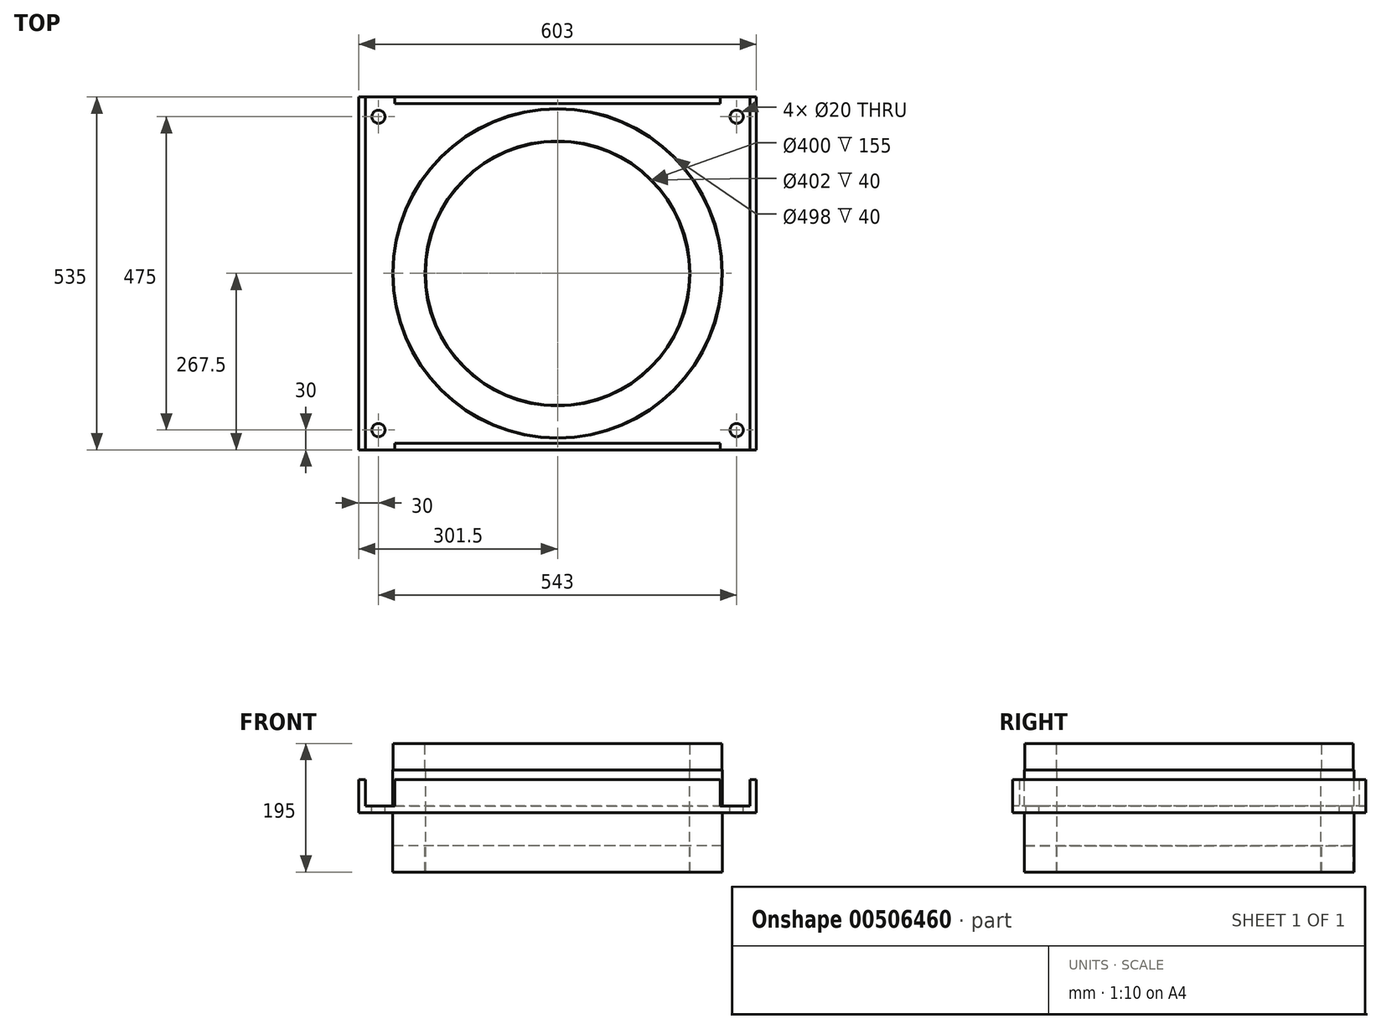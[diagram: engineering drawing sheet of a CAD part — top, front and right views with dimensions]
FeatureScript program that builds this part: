
annotation { "Feature Type Name" : "Feature", "Feature Type Description" : "" }
export const myFeature = defineFeature(function(context is Context, id is Id, definition is map)
    precondition{}
    {
        {
            var Q0;
            Q0=qCreatedBy(makeId("Front.planeOp"),FACE);
            var sketch = newSketch(context, id + "F0", { "sketchPlane" : qUnion([Q0])});
            skLineSegment(sketch, "E0", {"start": v(0, 74.87) * mm, "end": v(0, -73.71) * mm, "construction": true});
            skLineSegment(sketch, "E1", {"start": v(0, 374.84) * mm, "end": v(0, -528.94) * mm, "construction": true});
            skLineSegment(sketch, "E2", {"start": v(-200, -100) * mm, "end": v(-200, 55) * mm});
            skLineSegment(sketch, "E3", {"start": v(-200, 55) * mm, "end": v(-201, 55) * mm});
            skLineSegment(sketch, "E4", {"start": v(-201, 55) * mm, "end": v(-201, 95) * mm});
            skLineSegment(sketch, "E5", {"start": v(-201, 95) * mm, "end": v(-249, 95) * mm});
            skLineSegment(sketch, "E6", {"start": v(-249, 95) * mm, "end": v(-249, 55) * mm});
            skLineSegment(sketch, "E7", {"start": v(-249, 55) * mm, "end": v(-250, 55) * mm});
            skLineSegment(sketch, "E8", {"start": v(-250, 55) * mm, "end": v(-250, -100) * mm});
            skLineSegment(sketch, "E9", {"start": v(-250, -100) * mm, "end": v(-249, -100) * mm});
            skLineSegment(sketch, "E10", {"start": v(-249, -100) * mm, "end": v(-249, -60) * mm});
            skLineSegment(sketch, "E11", {"start": v(-249, -60) * mm, "end": v(-201, -60) * mm});
            skLineSegment(sketch, "E12", {"start": v(-201, -60) * mm, "end": v(-201, -100) * mm});
            skLineSegment(sketch, "E13", {"start": v(-201, -100) * mm, "end": v(-200, -100) * mm});
            skSolve(sketch);
        }
        {
            var Q0;
            Q0=qSketchRegion(id+"F0",true);
            var Q1;
            Q1=sQuery(id+"F0.wireOp",EDGE,"E1");
            revolve(context, id + "F1", {"entities" : qUnion([Q0]), "axis" : qUnion([Q1]), "revolveType" : RevolveType.FULL});
        }
        {
            var Q0;
            Q0=qCreatedBy(makeId("Top.planeOp"),FACE);
            var sketch = newSketch(context, id + "F2", { "sketchPlane" : qUnion([Q0])});
            skLineSegment(sketch, "E14.bottom", {"start": v(301.5, 267.5) * mm, "end": v(-301.5, 267.5) * mm});
            skLineSegment(sketch, "E14.top", {"start": v(301.5, -267.5) * mm, "end": v(-301.5, -267.5) * mm});
            skLineSegment(sketch, "E14.left", {"start": v(301.5, 267.5) * mm, "end": v(301.5, -267.5) * mm});
            skLineSegment(sketch, "E14.right", {"start": v(-301.5, 267.5) * mm, "end": v(-301.5, -267.5) * mm});
            skPoint(sketch, "E14.middle", {"position": v(0, 0) * mm});
            skCircle(sketch, "E15.0", {"center": v(0, 0) * mm, "radius": 201 * mm});
            skCircle(sketch, "E16.0", {"center": v(0, 0) * mm, "radius": 200 * mm});
            skLineSegment(sketch, "E17", {"start": v(0, 0) * mm, "end": v(0, 773.78) * mm, "construction": true});
            skLineSegment(sketch, "E18", {"start": v(0, 0) * mm, "end": v(1007.48, 0) * mm, "construction": true});
            skCircle(sketch, "E19", {"center": v(271.5, 237.5) * mm, "radius": 10 * mm});
            skCircle(sketch, "E20.MirrorC", {"center": v(-271.5, 237.5) * mm, "radius": 10 * mm});
            skCircle(sketch, "E21.MirrorC", {"center": v(271.5, -237.5) * mm, "radius": 10 * mm});
            skCircle(sketch, "E22.MirrorC", {"center": v(-271.5, -237.5) * mm, "radius": 10 * mm});
            skSolve(sketch);
        }
        {
            var Q0;
            Q0=qSketchRegion(id+"F2",true);
            extrude(context, id + "F3", {"entities" : qUnion([Q0]), "operationType" : NewBodyOperationType.ADD, "oppositeDirection" : true, "depth" : 10 * mm});
        }
        {
            var Q0;
            Q0=makeQuery(id+"F3.opExtrude","CAP_FACE",FACE,{"disambiguationData":[OSD([sQuery(id+"F2.wireOp",EDGE,"E14.bottom"),sQuery(id+"F2.wireOp",EDGE,"E14.top"),sQuery(id+"F2.wireOp",EDGE,"E14.left"),sQuery(id+"F2.wireOp",EDGE,"E14.right"),sQuery(id+"F2.wireOp",EDGE,"E16.0"),sQuery(id+"F2.wireOp",EDGE,"E19"),sQuery(id+"F2.wireOp",EDGE,"E20.MirrorC"),sQuery(id+"F2.wireOp",EDGE,"E21.MirrorC"),sQuery(id+"F2.wireOp",EDGE,"E22.MirrorC")])],"isStart":false});
            var sketch = newSketch(context, id + "F4", { "sketchPlane" : qUnion([Q0])});
            skLineSegment(sketch, "E23", {"start": v(0, 0) * mm, "end": v(-1098.02, 0) * mm, "construction": true});
            skLineSegment(sketch, "E24", {"start": v(0, 0) * mm, "end": v(0, -1084.2) * mm, "construction": true});
            skLineSegment(sketch, "E25.bottom", {"start": v(246.5, 267.5) * mm, "end": v(-246.5, 267.5) * mm});
            skLineSegment(sketch, "E25.top", {"start": v(246.5, 257.5) * mm, "end": v(-246.5, 257.5) * mm});
            skLineSegment(sketch, "E25.left", {"start": v(246.5, 267.5) * mm, "end": v(246.5, 257.5) * mm});
            skLineSegment(sketch, "E25.right", {"start": v(-246.5, 267.5) * mm, "end": v(-246.5, 257.5) * mm});
            skLineSegment(sketch, "E26.bottom", {"start": v(-301.5, 267.5) * mm, "end": v(-291.5, 267.5) * mm});
            skLineSegment(sketch, "E26.top", {"start": v(-301.5, -267.5) * mm, "end": v(-291.5, -267.5) * mm});
            skLineSegment(sketch, "E26.left", {"start": v(-301.5, 267.5) * mm, "end": v(-301.5, -267.5) * mm});
            skLineSegment(sketch, "E26.right", {"start": v(-291.5, 267.5) * mm, "end": v(-291.5, -267.5) * mm});
            skLineSegment(sketch, "E27.MirrorCS", {"start": v(246.5, -267.5) * mm, "end": v(246.5, -257.5) * mm});
            skLineSegment(sketch, "E28.MirrorCS", {"start": v(-246.5, -267.5) * mm, "end": v(-246.5, -257.5) * mm});
            skLineSegment(sketch, "E29.MirrorCS", {"start": v(246.5, -257.5) * mm, "end": v(-246.5, -257.5) * mm});
            skLineSegment(sketch, "E30.MirrorCS", {"start": v(246.5, -267.5) * mm, "end": v(-246.5, -267.5) * mm});
            skLineSegment(sketch, "E31.MirrorCS", {"start": v(301.5, -267.5) * mm, "end": v(291.5, -267.5) * mm});
            skLineSegment(sketch, "E32.MirrorCS", {"start": v(301.5, 267.5) * mm, "end": v(291.5, 267.5) * mm});
            skLineSegment(sketch, "E33.MirrorCS", {"start": v(301.5, 267.5) * mm, "end": v(301.5, -267.5) * mm});
            skLineSegment(sketch, "E34.MirrorCS", {"start": v(291.5, 267.5) * mm, "end": v(291.5, -267.5) * mm});
            skLineSegment(sketch, "E35.MirrorCS", {"start": v(0, 0) * mm, "end": v(1098.02, 0) * mm, "construction": true});
            skSolve(sketch);
        }
        {
            var Q0;
            Q0=qSketchRegion(id+"F4",true);
            extrude(context, id + "F5", {"entities" : qUnion([Q0]), "operationType" : NewBodyOperationType.ADD, "oppositeDirection" : true, "depth" : 50 * mm, "offsetDistance" : 25 * mm});
        }
    });
